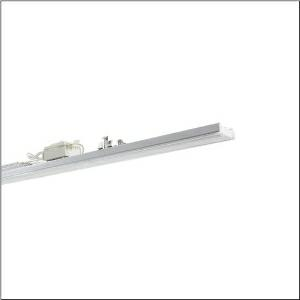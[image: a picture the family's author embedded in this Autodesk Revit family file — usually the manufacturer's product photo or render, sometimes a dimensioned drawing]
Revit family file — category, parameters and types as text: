
# Revit family: licross_r__21_recessed_mo_52tl11dn68xg3s_a87a
name_source: partatom
category: Lighting Fixtures
units: mm (PartAtom-declared; Revit-internal decimal feet)

## family parameters
Cut with Voids When Loaded = No
Host = Face
Light Source = No
Part Type = Normal
Room Calculation Point = No
Round Connector Dimension = Use Diameter
Shared = No

## types (1)
- --- (1 x LED, 910 lm, 6.7 W, 6500K)
    Apparent Load = 7 VA
    CIE Flux Codes = 89 96 99 100 100
    Color Rendering = 80
    Color Temperature = 6500K
    Default Elevation = 1800 mm
    Description = Licross® 21 Recessed MO, luminaire insert, of sheet steel, galvanised, coil coated, white, length: 1.500mm, width: 66mm, height: 67mm, LED rated luminous flux: 8.000lm, light colour: 865, control gear: DALI 2 (for two DALI lines), with plug, 6-pole, with phase selection, for trunking rail, 14-core, mains connection: 220..240V, AC, 50/60Hz, rated input power: 46W, for emergency light function, halogen-free wiring, for trunking rail, 14-core, converter,control gear: single battery element, battery: LiFePO4, 9Ah, primary optical cover: cover, of PMMA, light emission: direct distribution, primary light characteristic: symmetric, protection rating (complete): IP40, insulation class (complete): insulation class I (protective earthing), certification: CE, UKCA, protection symbol: D if used in an environment without relevant dust loads with corresponding accessories, impact resistance: IK06, permissible ambient temperature for indoor applications: +5..+35°C, standard: EN 60598-2-22, corresponds to IFS (International Featured Standards) requirements for safety and quality in the food industry, reducing of maximum allowable ambient temperature of 5°C with ceiling mounting, LABS conformity tested according to VDMA 24364:2018-05, packaging unit: 1 piece
    Height = 58 mm
    Lamp = 1 x LED
    Lamp Light Flux = 910 lm
    Lamp Power = 6.7 W
    Lamp count = 1
    Length = 1500 mm
    Luminous efficacy = 136 lm/W
    Manufacturer = Siteco
    ModVariant = No
    Model = 52TL11DN68XG3S
    Mounting Place = Ceiling
    Mounting Type = Pendant
    Number of Poles = 1
    OnlyDefault = Yes
    Power Factor = 1
    Product Name = Licross® 21 Recessed MO
    Product group = luminaire insert
    ProductGroupID = 902
    Protection Class = Protection class I
    Protection Degree = IP 40
    RLX_Detail_Level = 1
    RLX_Emergency_Light_Flux = 0 lm
    RLX_Emergency_Type = 0
    RLX_Emergency_Type_DB = No
    RlxData = <blob elided: 24921 chars, md5=83fd7ba9>
    Socket = socket
    Standby Power = 0 W
    System Light Flux = 910 lm
    System Power = 7 W
    Type Comments = : emergency light operation: 3 h
    Type Image = l_1296930.jpg
    URL = http://relux.com
    VarID = @adj_010361
    Voltage = 0 V
    Weight = 0.00 kg
    Width = 66 mm

## geometry (parser evidence)
native form markers: Blend x4, Sweep x9
no freeform markers — native parametric forms only
